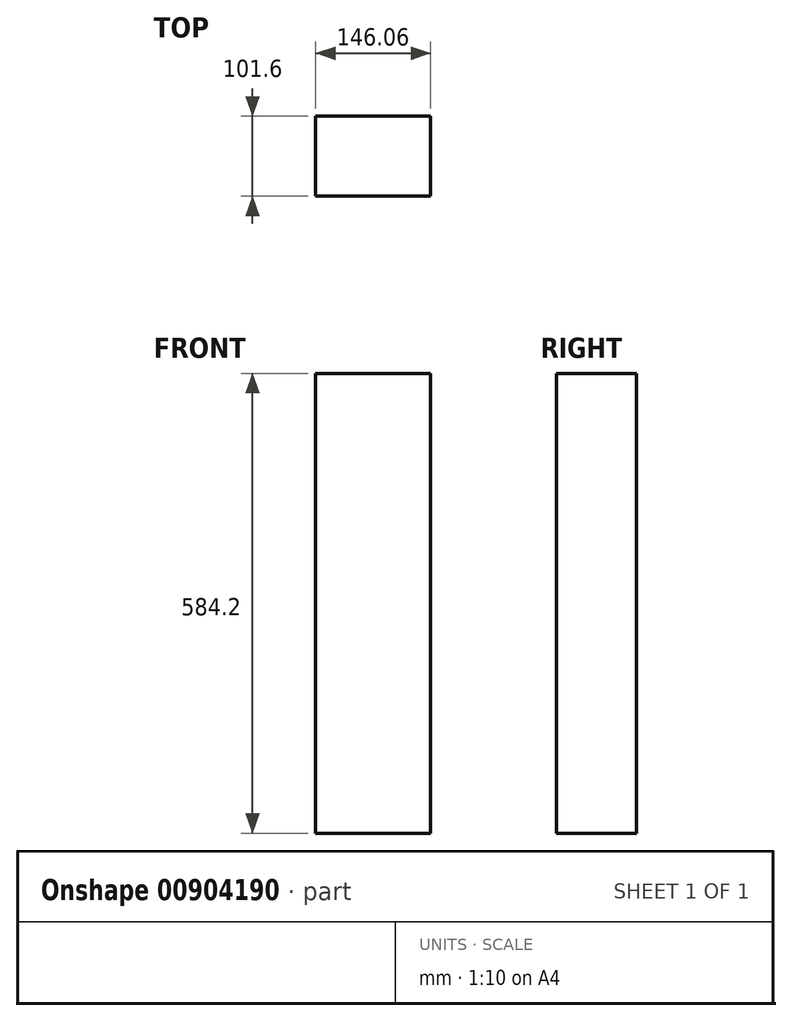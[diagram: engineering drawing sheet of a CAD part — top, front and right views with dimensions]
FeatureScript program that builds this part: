
annotation { "Feature Type Name" : "Feature", "Feature Type Description" : "" }
export const myFeature = defineFeature(function(context is Context, id is Id, definition is map)
    precondition{}
    {
        {
            var Q0;
            Q0=qCreatedBy(makeId("Top.planeOp"),FACE);
            var sketch = newSketch(context, id + "F0", { "sketchPlane" : qUnion([Q0])});
            skLineSegment(sketch, "E0.bottom", {"start": v(73.03, -50.8) * mm, "end": v(-73.02, -50.8) * mm});
            skLineSegment(sketch, "E0.top", {"start": v(73.02, 50.8) * mm, "end": v(-73.03, 50.8) * mm});
            skLineSegment(sketch, "E0.left", {"start": v(73.03, -50.8) * mm, "end": v(73.02, 50.8) * mm});
            skLineSegment(sketch, "E0.right", {"start": v(-73.02, -50.8) * mm, "end": v(-73.03, 50.8) * mm});
            skPoint(sketch, "E0.middle", {"position": v(0, 0) * mm});
            skSolve(sketch);
        }
        {
            var Q0;
            Q0=makeQuery(id+"F0.imprint","IMPRINT",FACE,{"disambiguationData":[TD([[makeQuery(id+"F0.imprint","IMPRINT",EDGE,{"derivedFrom":sQuery(id+"F0.wireOp",EDGE,"E0.bottom")}),-1.0]])]});
            extrude(context, id + "F1", {"entities" : qUnion([Q0]), "depth" : 584.2 * mm, "offsetDistance" : 25.4 * mm});
        }
        {
            var Q0;
            Q0=makeQuery(id+"F1.opExtrude","SWEPT_FACE",FACE,{"disambiguationData":[OSD([sQuery(id+"F0.wireOp",EDGE,"E0.top")])]});
            var sketch = newSketch(context, id + "F2", { "sketchPlane" : qUnion([Q0])});
            skLineSegment(sketch, "E1.0", {"start": v(-73.02, 146.05) * mm, "end": v(73.03, 146.05) * mm});
            skLineSegment(sketch, "E2.0", {"start": v(-73.02, 438.15) * mm, "end": v(73.03, 438.15) * mm});
            skCircle(sketch, "E3", {"center": v(0, 146.05) * mm, "radius": 6.35 * mm});
            skCircle(sketch, "E4", {"center": v(0, 438.15) * mm, "radius": 6.35 * mm});
            skSolve(sketch);
        }
        {
            var Q0;
            Q0=sQuery(id+"F2.wireOp",EDGE,"E3");
            extrude(context, id + "F3", {"bodyType" : ToolBodyType.SURFACE, "surfaceEntities" : qUnion([Q0]), "oppositeDirection" : true, "depth" : 101.6 * mm, "offsetDistance" : 25.4 * mm});
        }
    });
